# Revit family: Haworth_Cultivate_Table_BaseOnly
name_source: partatom
category: Furniture Systems
revit_build: Autodesk Revit 2018 (Build: 20170223_1515(x64)
units: mm (PartAtom-declared; Revit-internal decimal feet)

## family parameters
Always vertical = Yes
Cut with Voids When Loaded = No
OmniClass Number = 23.40.70.14.64.21
OmniClass Title = Systems Furniture
Part Type = Normal
Room Calculation Point = No
Round Connector Dimension = Use Diameter
Shared = No
Work Plane-Based = No

## types (1)
- 42h 72w 36d - Top Overhang - None
    Actual Depth = 36"
    Actual Height = 42"
    Actual Top Overhang - Both Sides - 19 in. = 0"
    Actual Top Overhang - Both Sides - 24 in. = 0"
    Actual Top Overhang - Left Side = 0"
    Actual Top Overhang - Right Side = 0"
    Actual Top Overhang - Right Side - 19 in. = 0"
    Actual Top Overhang - Right Side - 24 in. = 0"
    Actual Width = 72"
    Assembly Code = E2020200
    Bag Hook = No
    Bag Hook Finish = Haworth _ Paint _ Metallic Champagne
    Base Only = No
    Custom Size = No
    Depth = 36"
    Description = Haworth - Cultivate Table
    Footrest x1 = No
    Footrest x2 = Yes
    Frame Height = 40"
    Frame Height 28 in. = No
    Frame Height 40 in. = Yes
    Manufacturer = Haworth
    Max. Depth = 42"
    Max. Width = 134"
    Min. Depth = 36"
    Min. Width = 60"
    Min/Max Width = 60-120 in.; or 79-115 in.; or 98-134 in. @ 12 in. increments
    Model = Haworth - Cultivate Table
    Revision Number = 1
    Size = Verify Final Dim. w/ Haworth
    Standard Depths = 36, 42 in.
    Standard Height = 29, 30, 41, 41 in.
    Standard Top Thickness = 1 3/16, 2 in.
    Support Finish = Haworth _ Paint _ Metallic Champagne
    Support Height = 40"
    Sustainability Info = https://www.haworth.com
    Table Seam = No
    Top Included = Yes
    Top Overhang - Both Sides - 19 in. = No
    Top Overhang - Both Sides - 24 in. = No
    Top Overhang - None = Yes
    Top Overhang - Right Side - 19 in. = No
    Top Overhang - Right Side - 24 in. = No
    Top Thickness = 2"
    Top Thickness 1 3/16 in. = No
    Top Thickness 2 in. = Yes
    URL = www.haworth.com
    URL - Product = http://www.haworth.com
    Vertical Wire Manager = No
    Warranty = http://www.haworth.com
    Width = 72"
    Wire Manager Height = 37 53/64"

## geometry (parser evidence)
native form markers: Sweep x2
no freeform markers — native parametric forms only
